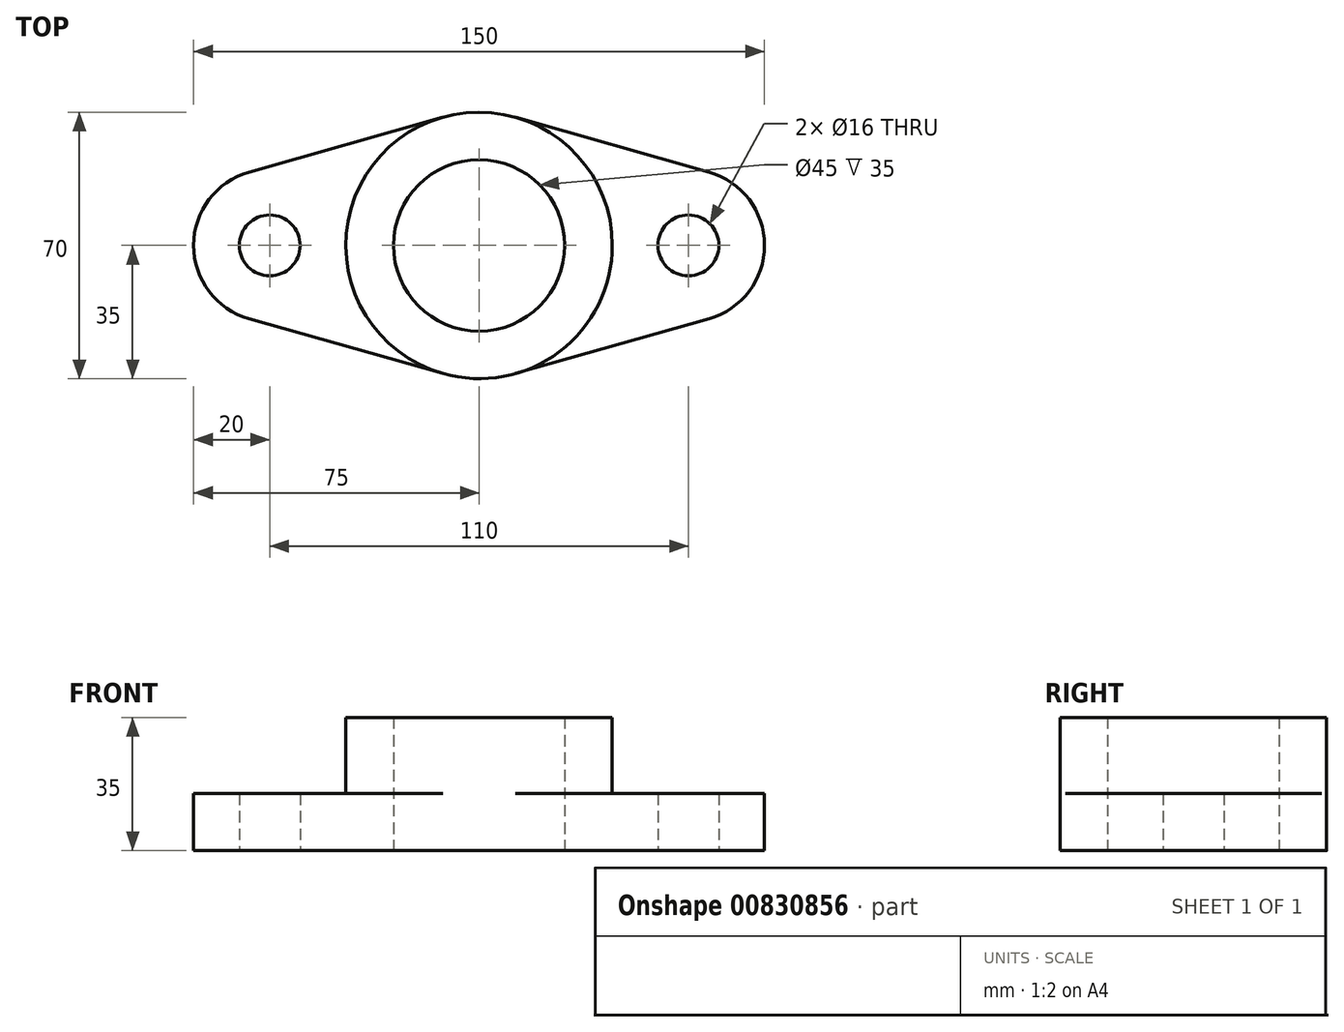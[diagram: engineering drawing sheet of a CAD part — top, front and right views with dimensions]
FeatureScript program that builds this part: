
annotation { "Feature Type Name" : "Feature", "Feature Type Description" : "" }
export const myFeature = defineFeature(function(context is Context, id is Id, definition is map)
    precondition{}
    {
        {
            var Q0;
            Q0=qCreatedBy(makeId("Top.planeOp"),FACE);
            var sketch = newSketch(context, id + "F0", { "sketchPlane" : qUnion([Q0])});
            skCircle(sketch, "E0", {"center": v(0, 0) * mm, "radius": 22.5 * mm});
            skCircle(sketch, "E1", {"center": v(-55, 0) * mm, "radius": 8 * mm});
            skCircle(sketch, "E2", {"center": v(55, 0) * mm, "radius": 8 * mm});
            skCircle(sketch, "E3", {"center": v(-55, 0) * mm, "radius": 20 * mm});
            skCircle(sketch, "E4", {"center": v(55, 0) * mm, "radius": 20 * mm});
            skCircle(sketch, "E5", {"center": v(0, 0) * mm, "radius": 35 * mm});
            skLineSegment(sketch, "E6", {"start": v(-9.55, 33.67) * mm, "end": v(-60.45, 19.24) * mm});
            skLineSegment(sketch, "E7", {"start": v(-60.45, -19.24) * mm, "end": v(-9.55, -33.67) * mm});
            skLineSegment(sketch, "E8", {"start": v(9.55, 33.67) * mm, "end": v(60.45, 19.24) * mm});
            skLineSegment(sketch, "E9", {"start": v(9.55, -33.67) * mm, "end": v(60.45, -19.24) * mm});
            skSolve(sketch);
        }
        {
            var Q0;
            {var subQ0=sQuery(id+"F0.wireOp",EDGE,"E6");Q0=makeQuery(id+"F0.imprint","IMPRINT",FACE,{"disambiguationData":[TD([[makeQuery(id+"F0.imprint","IMPRINT",EDGE,{"derivedFrom":subQ0}),1.0]])]});}
            var Q1;
            {var subQ0=sQuery(id+"F0.wireOp",EDGE,"E7");Q1=makeQuery(id+"F0.imprint","IMPRINT",FACE,{"disambiguationData":[TD([[makeQuery(id+"F0.imprint","IMPRINT",EDGE,{"derivedFrom":subQ0}),1.0]])]});}
            var Q2;
            {var subQ0=sQuery(id+"F0.wireOp",EDGE,"E8");Q2=makeQuery(id+"F0.imprint","IMPRINT",FACE,{"disambiguationData":[TD([[makeQuery(id+"F0.imprint","IMPRINT",EDGE,{"derivedFrom":subQ0}),-1.0]])]});}
            var Q3;
            {var subQ0=sQuery(id+"F0.wireOp",EDGE,"E9");Q3=makeQuery(id+"F0.imprint","IMPRINT",FACE,{"disambiguationData":[TD([[makeQuery(id+"F0.imprint","IMPRINT",EDGE,{"derivedFrom":subQ0}),1.0]])]});}
            var Q4;
            Q4=makeQuery(id+"F0.imprint","IMPRINT",FACE,{"disambiguationData":[TD([[makeQuery(id+"F0.imprint","IMPRINT",EDGE,{"derivedFrom":sQuery(id+"F0.wireOp",EDGE,"E2")}),-1.0]])]});
            var Q5;
            Q5=makeQuery(id+"F0.imprint","IMPRINT",FACE,{"disambiguationData":[TD([[makeQuery(id+"F0.imprint","IMPRINT",EDGE,{"derivedFrom":sQuery(id+"F0.wireOp",EDGE,"E0")}),-1.0]])]});
            var Q6;
            Q6=makeQuery(id+"F0.imprint","IMPRINT",FACE,{"disambiguationData":[TD([[makeQuery(id+"F0.imprint","IMPRINT",EDGE,{"derivedFrom":sQuery(id+"F0.wireOp",EDGE,"E1")}),-1.0]])]});
            extrude(context, id + "F1", {"entities" : qUnion([Q0, Q1, Q2, Q3, Q4, Q5, Q6]), "depth" : 15 * mm, "offsetDistance" : 25 * mm});
        }
        {
            var Q0;
            Q0=makeQuery(id+"F1.opExtrude","CAP_FACE",FACE,{"disambiguationData":[OSD([sQuery(id+"F0.wireOp",EDGE,"E0"),sQuery(id+"F0.wireOp",EDGE,"E1"),sQuery(id+"F0.wireOp",EDGE,"E2"),sQuery(id+"F0.wireOp",EDGE,"E3"),sQuery(id+"F0.wireOp",EDGE,"E4"),sQuery(id+"F0.wireOp",EDGE,"E5"),sQuery(id+"F0.wireOp",EDGE,"E6"),sQuery(id+"F0.wireOp",EDGE,"E7"),sQuery(id+"F0.wireOp",EDGE,"E8"),sQuery(id+"F0.wireOp",EDGE,"E9")])],"isStart":false});
            var sketch = newSketch(context, id + "F2", { "sketchPlane" : qUnion([Q0])});
            skCircle(sketch, "E10", {"center": v(0, 0) * mm, "radius": 22.5 * mm});
            skCircle(sketch, "E11", {"center": v(0, 0) * mm, "radius": 35 * mm});
            skSolve(sketch);
        }
        {
            var Q0;
            Q0=makeQuery(id+"F2.imprint","IMPRINT",FACE,{"disambiguationData":[TD([[makeQuery(id+"F2.imprint","IMPRINT",EDGE,{"derivedFrom":sQuery(id+"F2.wireOp",EDGE,"E10")}),-1.0]])]});
            extrude(context, id + "F3", {"entities" : qUnion([Q0]), "operationType" : NewBodyOperationType.ADD, "depth" : 20 * mm, "offsetDistance" : 25 * mm});
        }
    });
